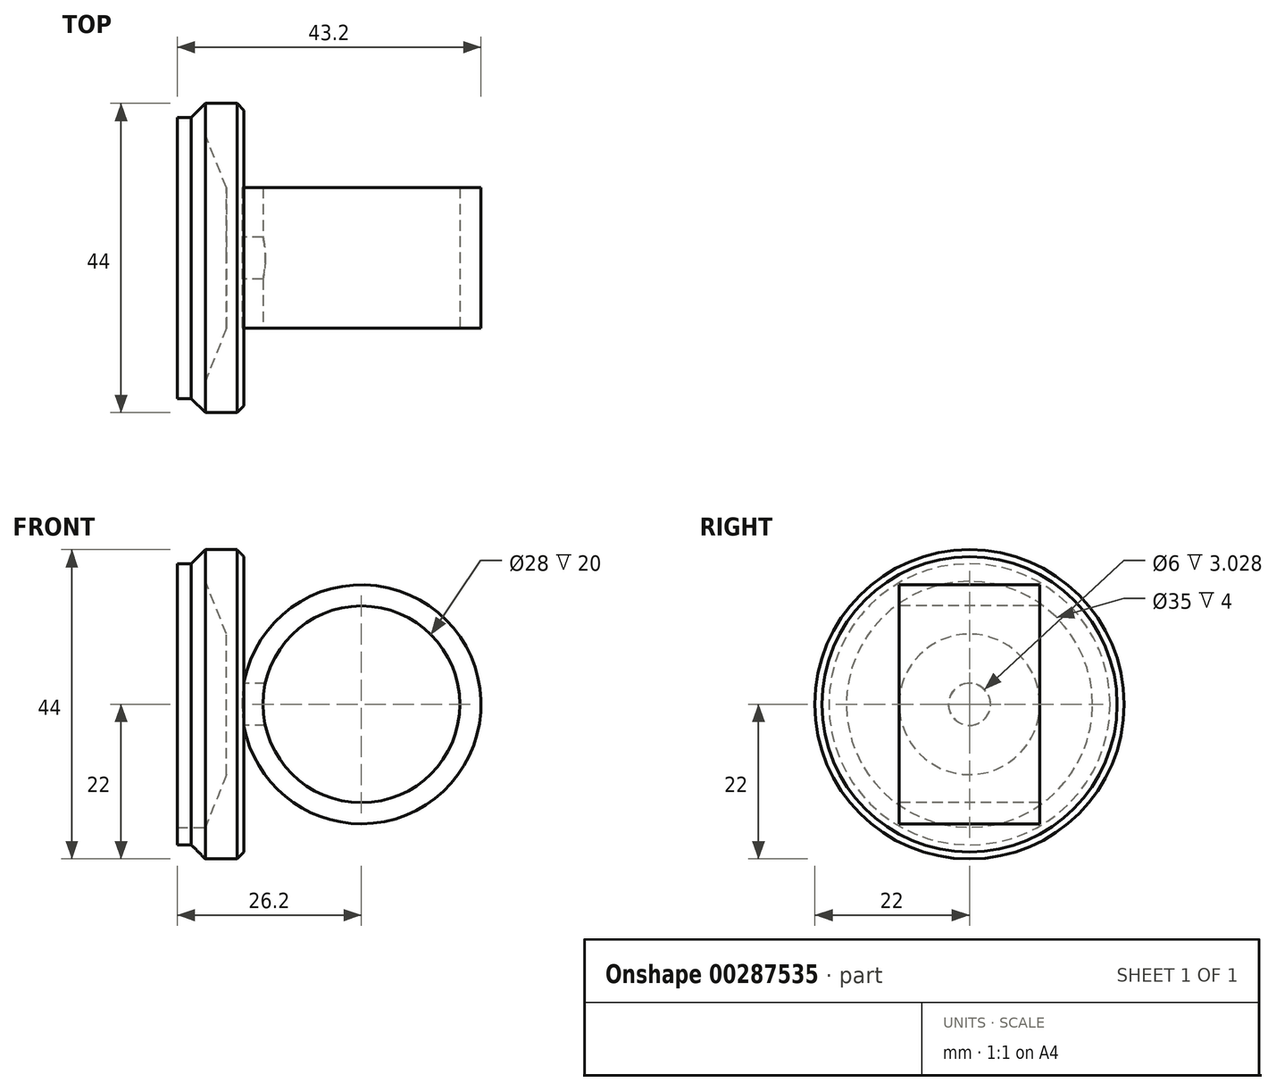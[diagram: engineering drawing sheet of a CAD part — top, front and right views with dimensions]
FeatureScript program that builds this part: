
annotation { "Feature Type Name" : "Feature", "Feature Type Description" : "" }
export const myFeature = defineFeature(function(context is Context, id is Id, definition is map)
    precondition{}
    {
        {
            var Q0;
            Q0=qCreatedBy(makeId("Front.planeOp"),FACE);
            var sketch = newSketch(context, id + "F0", { "sketchPlane" : qUnion([Q0])});
            skLineSegment(sketch, "E0", {"start": v(0, 0) * mm, "end": v(0, 20) * mm});
            skPoint(sketch, "E1", {"position": v(0, 17.5) * mm});
            skLineSegment(sketch, "E2", {"start": v(0, 20) * mm, "end": v(2, 20) * mm});
            skLineSegment(sketch, "E3", {"start": v(2, 20) * mm, "end": v(2, 22) * mm});
            skLineSegment(sketch, "E4", {"start": v(2, 22) * mm, "end": v(9.5, 22) * mm});
            skLineSegment(sketch, "E5", {"start": v(9.5, 22) * mm, "end": v(9.5, 0) * mm});
            skLineSegment(sketch, "E6", {"start": v(9.5, 0) * mm, "end": v(0, 0) * mm});
            skPoint(sketch, "E7", {"position": v(4, 17.5) * mm});
            skPoint(sketch, "E8", {"position": v(7, 17.5) * mm});
            skLineSegment(sketch, "E9", {"start": v(7, 0) * mm, "end": v(7, 10) * mm});
            skLineSegment(sketch, "E10", {"start": v(7, 10) * mm, "end": v(4, 17.5) * mm});
            skLineSegment(sketch, "E11", {"start": v(0, 17.5) * mm, "end": v(4, 17.5) * mm});
            skLineSegment(sketch, "E12", {"start": v(9.5, 0) * mm, "end": v(12.5, 0) * mm});
            skLineSegment(sketch, "E13", {"start": v(12.5, 0) * mm, "end": v(12.5, 3) * mm});
            skLineSegment(sketch, "E14", {"start": v(12.5, 3) * mm, "end": v(9.5, 3) * mm});
            skSolve(sketch);
        }
        {
            var Q0;
            {var subQ0=sQuery(id+"F0.wireOp",EDGE,"E2");Q0=makeQuery(id+"F0.imprint","IMPRINT",FACE,{"disambiguationData":[TD([[makeQuery(id+"F0.imprint","IMPRINT",EDGE,{"derivedFrom":subQ0}),-1.0]])]});}
            var Q1;
            {var subQ0=sQuery(id+"F0.wireOp",EDGE,"E12");Q1=makeQuery(id+"F0.imprint","IMPRINT",FACE,{"disambiguationData":[TD([[makeQuery(id+"F0.imprint","IMPRINT",EDGE,{"derivedFrom":subQ0}),1.0]])]});}
            var Q2;
            Q2=sQuery(id+"F0.wireOp",EDGE,"E6");
            revolve(context, id + "F1", {"entities" : qUnion([Q0, Q1]), "axis" : qUnion([Q2]), "revolveType" : RevolveType.FULL});
        }
        {
            var Q0;
            Q0=makeQuery(id+"F1.opRevolve","SWEPT_EDGE",EDGE,{"disambiguationData":[OSD([sQuery(id+"F0.wireOp",EDGE,"E3"),sQuery(id+"F0.wireOp",EDGE,"E4")])]});
            chamfer(context, id + "F2", {"entities" : qUnion([Q0]), "width" : 2 * mm, "tangentPropagation" : true});
        }
        {
            var Q0;
            Q0=qCreatedBy(makeId("Front.planeOp"),FACE);
            cPlane(context, id + "F3", {"entities" : qUnion([Q0]), "cplaneType" : CPlaneType.OFFSET, "offset" : 10 * mm, "width" : 150 * mm, "height" : 150 * mm});
        }
        {
            var Q0;
            Q0=qCreatedBy(id+"F3.planeOp",FACE);
            var sketch = newSketch(context, id + "F4", { "sketchPlane" : qUnion([Q0])});
            skPoint(sketch, "E15", {"position": v(26.2, 0) * mm});
            skCircle(sketch, "E16", {"center": v(26.2, 0) * mm, "radius": 17 * mm});
            skCircle(sketch, "E17", {"center": v(26.2, 0) * mm, "radius": 14 * mm});
            skSolve(sketch);
        }
        {
            var Q0;
            Q0=qSketchRegion(id+"F4",true);
            extrude(context, id + "F5", {"entities" : qUnion([Q0]), "oppositeDirection" : true, "depth" : 20 * mm});
        }
        {
            var Q0;
            Q0=qCreatedBy(makeId("Right.planeOp"),FACE);
            cPlane(context, id + "F6", {"entities" : qUnion([Q0]), "cplaneType" : CPlaneType.OFFSET, "offset" : 9.5 * mm, "width" : 150 * mm, "height" : 150 * mm});
        }
        {
            var Q0;
            Q0=qCreatedBy(id+"F6.planeOp",FACE);
            var sketch = newSketch(context, id + "F7", { "sketchPlane" : qUnion([Q0])});
            skCircle(sketch, "E18", {"center": v(0, 0) * mm, "radius": 3 * mm});
            skSolve(sketch);
        }
        {
            var Q0;
            Q0=qSketchRegion(id+"F7",true);
            extrude(context, id + "F8", {"entities" : qUnion([Q0]), "operationType" : NewBodyOperationType.REMOVE, "depth" : 5 * mm});
        }
        {
            var Q0;
            Q0=makeQuery(id+"F1.opRevolve","SWEPT_EDGE",EDGE,{"disambiguationData":[OSD([sQuery(id+"F0.wireOp",EDGE,"E4"),sQuery(id+"F0.wireOp",EDGE,"E5")])]});
            chamfer(context, id + "F9", {"entities" : qUnion([Q0]), "width" : 1 * mm, "tangentPropagation" : true});
        }
    });
